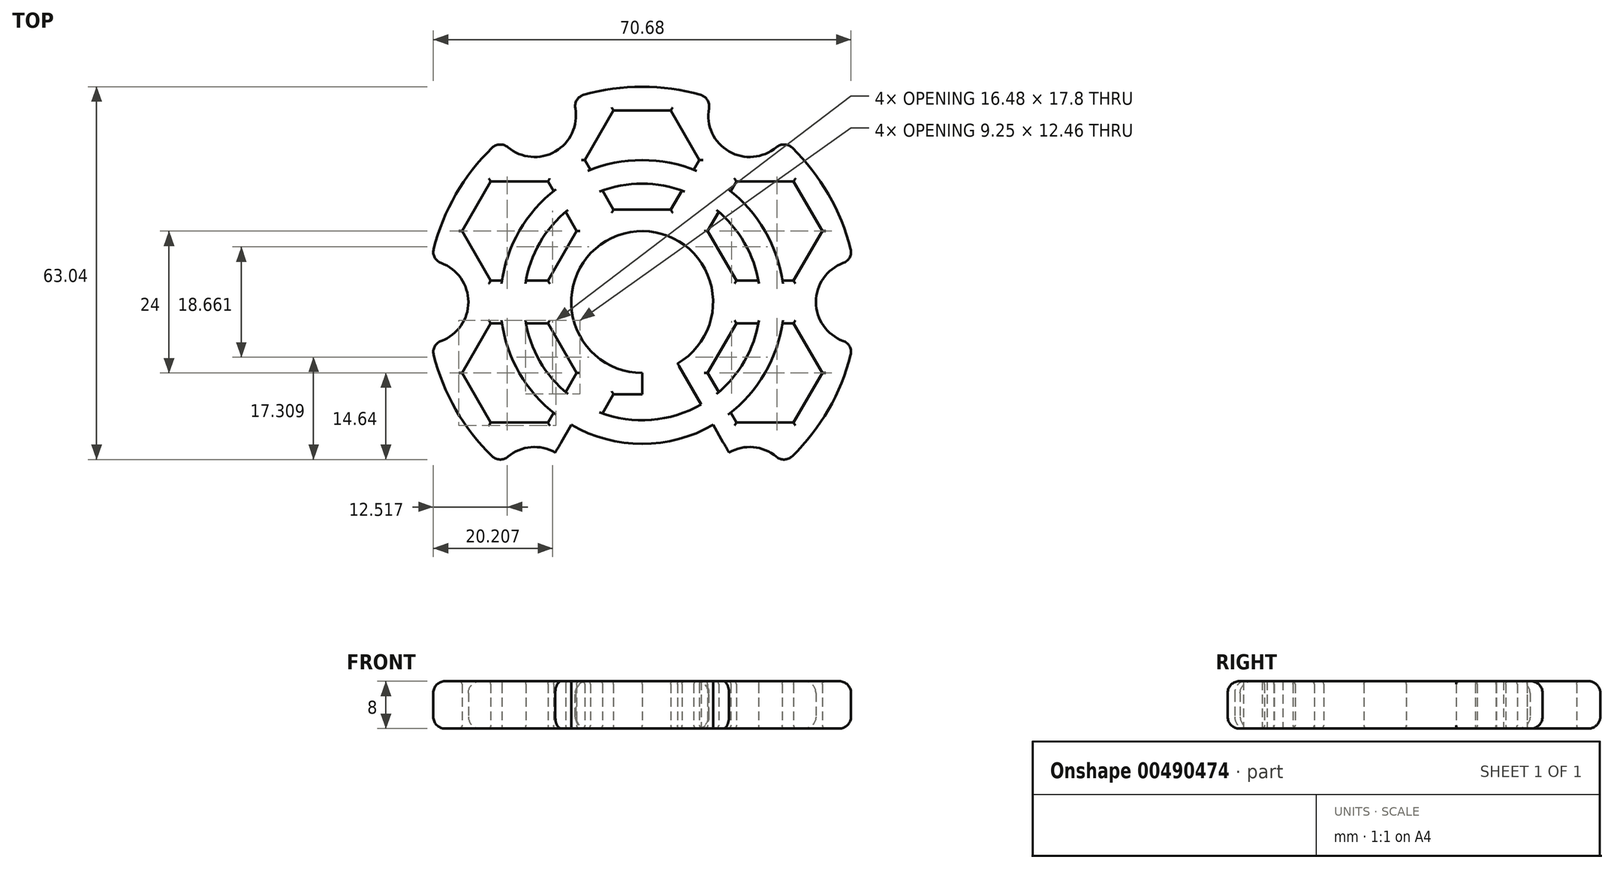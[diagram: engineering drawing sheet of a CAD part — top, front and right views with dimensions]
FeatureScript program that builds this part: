
annotation { "Feature Type Name" : "Feature", "Feature Type Description" : "" }
export const myFeature = defineFeature(function(context is Context, id is Id, definition is map)
    precondition{}
    {
        {
            var Q0;
            Q0=qCreatedBy(makeId("Top.planeOp"),FACE);
            var sketch = newSketch(context, id + "F0", { "sketchPlane" : qUnion([Q0])});
            skCircle(sketch, "E0", {"center": v(0, 0) * mm, "radius": 12 * mm});
            skCircle(sketch, "E1", {"center": v(0, 0) * mm, "radius": 20 * mm});
            skLineSegment(sketch, "E2", {"start": v(0, 0) * mm, "end": v(0, -49.72) * mm});
            skLineSegment(sketch, "E3", {"start": v(0, -49.72) * mm, "end": v(0, 47.4) * mm});
            skLineSegment(sketch, "E4", {"start": v(0, 0) * mm, "end": v(51.5, 29.74) * mm});
            skLineSegment(sketch, "E5", {"start": v(0, 0) * mm, "end": v(-51.59, -29.79) * mm});
            skLineSegment(sketch, "E6", {"start": v(0, 0) * mm, "end": v(55.92, -32.29) * mm});
            skLineSegment(sketch, "E7", {"start": v(0, 0) * mm, "end": v(-48.7, 28.11) * mm});
            skCircle(sketch, "E8", {"center": v(0, 0) * mm, "radius": 24 * mm});
            skCircle(sketch, "E9", {"center": v(0, 0) * mm, "radius": 36.4 * mm});
            skLineSegment(sketch, "E10", {"start": v(0, 0) * mm, "end": v(24.72, 42.82) * mm});
            skLineSegment(sketch, "E11", {"start": v(0, 0) * mm, "end": v(-26.3, -45.55) * mm});
            skLineSegment(sketch, "E12", {"start": v(0, 0) * mm, "end": v(-50.78, 0) * mm});
            skLineSegment(sketch, "E13", {"start": v(0, 0) * mm, "end": v(-24.9, 43.14) * mm});
            skLineSegment(sketch, "E14", {"start": v(0, 0) * mm, "end": v(57.78, 0) * mm});
            skLineSegment(sketch, "E15", {"start": v(0, 0) * mm, "end": v(28.24, -48.92) * mm});
            skCircle(sketch, "E16", {"center": v(18.2, 31.52) * mm, "radius": 7 * mm});
            skCircle(sketch, "E17", {"center": v(36.4, 0) * mm, "radius": 7 * mm});
            skCircle(sketch, "E18", {"center": v(18.2, -31.52) * mm, "radius": 7 * mm});
            skCircle(sketch, "E19", {"center": v(-18.2, -31.52) * mm, "radius": 7 * mm});
            skCircle(sketch, "E20", {"center": v(-36.4, 0) * mm, "radius": 7 * mm});
            skCircle(sketch, "E21", {"center": v(-18.2, 31.52) * mm, "radius": 7 * mm});
            skCircle(sketch, "E22.cCircle", {"center": v(0, -24) * mm, "radius": 8.4 * mm, "construction": true});
            skLineSegment(sketch, "E22.0", {"start": v(-4.85, -15.6) * mm, "end": v(4.85, -15.6) * mm});
            skLineSegment(sketch, "E22.1", {"start": v(4.85, -15.6) * mm, "end": v(9.7, -24) * mm});
            skLineSegment(sketch, "E22.2", {"start": v(9.7, -24) * mm, "end": v(4.85, -32.4) * mm});
            skLineSegment(sketch, "E22.3", {"start": v(4.85, -32.4) * mm, "end": v(-4.85, -32.4) * mm});
            skLineSegment(sketch, "E22.4", {"start": v(-4.85, -32.4) * mm, "end": v(-9.7, -24) * mm});
            skLineSegment(sketch, "E22.5", {"start": v(-9.7, -24) * mm, "end": v(-4.85, -15.6) * mm});
            skPoint(sketch, "E22.0.midPoint", {"position": v(0, -15.6) * mm});
            skCircle(sketch, "E23.cCircle", {"center": v(-20.78, -12) * mm, "radius": 8.4 * mm, "construction": true});
            skLineSegment(sketch, "E23.0", {"start": v(-15.93, -3.6) * mm, "end": v(-11.09, -12) * mm});
            skLineSegment(sketch, "E23.1", {"start": v(-11.09, -12) * mm, "end": v(-15.93, -20.4) * mm});
            skLineSegment(sketch, "E23.2", {"start": v(-15.93, -20.4) * mm, "end": v(-25.63, -20.4) * mm});
            skLineSegment(sketch, "E23.3", {"start": v(-25.63, -20.4) * mm, "end": v(-30.48, -12) * mm});
            skLineSegment(sketch, "E23.4", {"start": v(-30.48, -12) * mm, "end": v(-25.63, -3.6) * mm});
            skLineSegment(sketch, "E23.5", {"start": v(-25.63, -3.6) * mm, "end": v(-15.93, -3.6) * mm});
            skPoint(sketch, "E23.0.midPoint", {"position": v(-13.5, -7.8) * mm});
            skCircle(sketch, "E24.cCircle", {"center": v(-20.78, 12) * mm, "radius": 8.4 * mm, "construction": true});
            skLineSegment(sketch, "E24.0", {"start": v(-11.09, 12) * mm, "end": v(-15.93, 3.6) * mm});
            skLineSegment(sketch, "E24.1", {"start": v(-15.93, 3.6) * mm, "end": v(-25.63, 3.6) * mm});
            skLineSegment(sketch, "E24.2", {"start": v(-25.63, 3.6) * mm, "end": v(-30.48, 12) * mm});
            skLineSegment(sketch, "E24.3", {"start": v(-30.48, 12) * mm, "end": v(-25.63, 20.4) * mm});
            skLineSegment(sketch, "E24.4", {"start": v(-25.63, 20.4) * mm, "end": v(-15.93, 20.4) * mm});
            skLineSegment(sketch, "E24.5", {"start": v(-15.93, 20.4) * mm, "end": v(-11.09, 12) * mm});
            skPoint(sketch, "E24.0.midPoint", {"position": v(-13.5, 7.8) * mm});
            skCircle(sketch, "E25.cCircle", {"center": v(0, 24) * mm, "radius": 8.4 * mm, "construction": true});
            skLineSegment(sketch, "E25.0", {"start": v(4.85, 15.6) * mm, "end": v(-4.85, 15.6) * mm});
            skLineSegment(sketch, "E25.1", {"start": v(-4.85, 15.6) * mm, "end": v(-9.7, 24) * mm});
            skLineSegment(sketch, "E25.2", {"start": v(-9.7, 24) * mm, "end": v(-4.85, 32.4) * mm});
            skLineSegment(sketch, "E25.3", {"start": v(-4.85, 32.4) * mm, "end": v(4.85, 32.4) * mm});
            skLineSegment(sketch, "E25.4", {"start": v(4.85, 32.4) * mm, "end": v(9.7, 24) * mm});
            skLineSegment(sketch, "E25.5", {"start": v(9.7, 24) * mm, "end": v(4.85, 15.6) * mm});
            skPoint(sketch, "E25.0.midPoint", {"position": v(0, 15.6) * mm});
            skCircle(sketch, "E26.cCircle", {"center": v(20.78, 12) * mm, "radius": 8.4 * mm, "construction": true});
            skLineSegment(sketch, "E26.0", {"start": v(15.93, 3.6) * mm, "end": v(11.09, 12) * mm});
            skLineSegment(sketch, "E26.1", {"start": v(11.09, 12) * mm, "end": v(15.93, 20.4) * mm});
            skLineSegment(sketch, "E26.2", {"start": v(15.93, 20.4) * mm, "end": v(25.63, 20.4) * mm});
            skLineSegment(sketch, "E26.3", {"start": v(25.63, 20.4) * mm, "end": v(30.48, 12) * mm});
            skLineSegment(sketch, "E26.4", {"start": v(30.48, 12) * mm, "end": v(25.63, 3.6) * mm});
            skLineSegment(sketch, "E26.5", {"start": v(25.63, 3.6) * mm, "end": v(15.93, 3.6) * mm});
            skPoint(sketch, "E26.0.midPoint", {"position": v(13.5, 7.8) * mm});
            skCircle(sketch, "E27.cCircle", {"center": v(20.78, -12) * mm, "radius": 8.4 * mm, "construction": true});
            skLineSegment(sketch, "E27.0", {"start": v(11.09, -12) * mm, "end": v(15.93, -3.6) * mm});
            skLineSegment(sketch, "E27.1", {"start": v(15.93, -3.6) * mm, "end": v(25.63, -3.6) * mm});
            skLineSegment(sketch, "E27.2", {"start": v(25.63, -3.6) * mm, "end": v(30.48, -12) * mm});
            skLineSegment(sketch, "E27.3", {"start": v(30.48, -12) * mm, "end": v(25.63, -20.4) * mm});
            skLineSegment(sketch, "E27.4", {"start": v(25.63, -20.4) * mm, "end": v(15.93, -20.4) * mm});
            skLineSegment(sketch, "E27.5", {"start": v(15.93, -20.4) * mm, "end": v(11.09, -12) * mm});
            skPoint(sketch, "E27.0.midPoint", {"position": v(13.5, -7.8) * mm});
            skSolve(sketch);
        }
        {
            var Q0;
            {var subQ0=sQuery(id+"F0.wireOp",EDGE,"E9");var subQ1=sQuery(id+"F0.wireOp",EDGE,"E7");var subQ2=makeQuery(id+"F0.imprint","INTERSECT",VERTEX,{"derivedFrom":[subQ1,subQ0]});Q0=makeQuery(id+"F0.imprint","IMPRINT",FACE,{"disambiguationData":[TD([[makeQuery(id+"F0.imprint","IMPRINT",EDGE,{"disambiguationData":[TD([[subQ2,1.0]])],"derivedFrom":subQ1}),1.0]])]});}
            var Q1;
            {var subQ0=sQuery(id+"F0.wireOp",EDGE,"E9");var subQ1=sQuery(id+"F0.wireOp",EDGE,"E7");var subQ2=makeQuery(id+"F0.imprint","INTERSECT",VERTEX,{"derivedFrom":[subQ1,subQ0]});Q1=makeQuery(id+"F0.imprint","IMPRINT",FACE,{"disambiguationData":[TD([[makeQuery(id+"F0.imprint","IMPRINT",EDGE,{"disambiguationData":[TD([[subQ2,1.0]])],"derivedFrom":subQ1}),-1.0]])]});}
            var Q2;
            {var subQ1=sQuery(id+"F0.wireOp",EDGE,"E3");var subQ7=sQuery(id+"F0.wireOp",EDGE,"E9");var subQ8=makeQuery(id+"F0.imprint","INTERSECT",VERTEX,{"disambiguationData":[OD(1.0)],"derivedFrom":[subQ1,subQ7]});Q2=makeQuery(id+"F0.imprint","IMPRINT",FACE,{"disambiguationData":[TD([[makeQuery(id+"F0.imprint","IMPRINT",EDGE,{"disambiguationData":[TD([[subQ8,1.0]])],"derivedFrom":subQ1}),1.0]])]});}
            var Q3;
            {var subQ0=sQuery(id+"F0.wireOp",EDGE,"E9");var subQ1=sQuery(id+"F0.wireOp",EDGE,"E3");var subQ2=makeQuery(id+"F0.imprint","INTERSECT",VERTEX,{"disambiguationData":[OD(1.0)],"derivedFrom":[subQ1,subQ0]});Q3=makeQuery(id+"F0.imprint","IMPRINT",FACE,{"disambiguationData":[TD([[makeQuery(id+"F0.imprint","IMPRINT",EDGE,{"disambiguationData":[TD([[subQ2,1.0]])],"derivedFrom":subQ1}),-1.0]])]});}
            var Q4;
            {var subQ0=sQuery(id+"F0.wireOp",EDGE,"E9");var subQ1=sQuery(id+"F0.wireOp",EDGE,"E4");var subQ2=makeQuery(id+"F0.imprint","INTERSECT",VERTEX,{"derivedFrom":[subQ1,subQ0]});Q4=makeQuery(id+"F0.imprint","IMPRINT",FACE,{"disambiguationData":[TD([[makeQuery(id+"F0.imprint","IMPRINT",EDGE,{"disambiguationData":[TD([[subQ2,1.0]])],"derivedFrom":subQ1}),1.0]])]});}
            var Q5;
            {var subQ1=sQuery(id+"F0.wireOp",EDGE,"E4");var subQ9=sQuery(id+"F0.wireOp",EDGE,"E9");var subQ10=makeQuery(id+"F0.imprint","INTERSECT",VERTEX,{"derivedFrom":[subQ1,subQ9]});Q5=makeQuery(id+"F0.imprint","IMPRINT",FACE,{"disambiguationData":[TD([[makeQuery(id+"F0.imprint","IMPRINT",EDGE,{"disambiguationData":[TD([[subQ10,1.0]])],"derivedFrom":subQ1}),-1.0]])]});}
            var Q6;
            {var subQ0=sQuery(id+"F0.wireOp",EDGE,"E9");var subQ1=sQuery(id+"F0.wireOp",EDGE,"E6");var subQ2=makeQuery(id+"F0.imprint","INTERSECT",VERTEX,{"derivedFrom":[subQ1,subQ0]});Q6=makeQuery(id+"F0.imprint","IMPRINT",FACE,{"disambiguationData":[TD([[makeQuery(id+"F0.imprint","IMPRINT",EDGE,{"disambiguationData":[TD([[subQ2,1.0]])],"derivedFrom":subQ1}),1.0]])]});}
            var Q7;
            {var subQ1=sQuery(id+"F0.wireOp",EDGE,"E6");var subQ5=sQuery(id+"F0.wireOp",EDGE,"E9");var subQ6=makeQuery(id+"F0.imprint","INTERSECT",VERTEX,{"derivedFrom":[subQ1,subQ5]});Q7=makeQuery(id+"F0.imprint","IMPRINT",FACE,{"disambiguationData":[TD([[makeQuery(id+"F0.imprint","IMPRINT",EDGE,{"disambiguationData":[TD([[subQ6,1.0]])],"derivedFrom":subQ1}),-1.0]])]});}
            var Q8;
            {var subQ0=sQuery(id+"F0.wireOp",EDGE,"E9");var subQ1=sQuery(id+"F0.wireOp",EDGE,"E3");var subQ2=makeQuery(id+"F0.imprint","INTERSECT",VERTEX,{"disambiguationData":[OD(0.0)],"derivedFrom":[subQ1,subQ0]});Q8=makeQuery(id+"F0.imprint","IMPRINT",FACE,{"disambiguationData":[TD([[makeQuery(id+"F0.imprint","IMPRINT",EDGE,{"disambiguationData":[TD([[subQ2,-1.0]])],"derivedFrom":subQ1}),-1.0]])]});}
            var Q9;
            {var subQ1=sQuery(id+"F0.wireOp",EDGE,"E3");var subQ7=sQuery(id+"F0.wireOp",EDGE,"E9");var subQ8=makeQuery(id+"F0.imprint","INTERSECT",VERTEX,{"disambiguationData":[OD(0.0)],"derivedFrom":[subQ1,subQ7]});Q9=makeQuery(id+"F0.imprint","IMPRINT",FACE,{"disambiguationData":[TD([[makeQuery(id+"F0.imprint","IMPRINT",EDGE,{"disambiguationData":[TD([[subQ8,-1.0]])],"derivedFrom":subQ1}),1.0]])]});}
            var Q10;
            {var subQ0=sQuery(id+"F0.wireOp",EDGE,"E9");var subQ1=sQuery(id+"F0.wireOp",EDGE,"E5");var subQ2=makeQuery(id+"F0.imprint","INTERSECT",VERTEX,{"derivedFrom":[subQ1,subQ0]});Q10=makeQuery(id+"F0.imprint","IMPRINT",FACE,{"disambiguationData":[TD([[makeQuery(id+"F0.imprint","IMPRINT",EDGE,{"disambiguationData":[TD([[subQ2,1.0]])],"derivedFrom":subQ1}),1.0]])]});}
            var Q11;
            {var subQ0=sQuery(id+"F0.wireOp",EDGE,"E9");var subQ1=sQuery(id+"F0.wireOp",EDGE,"E5");var subQ2=makeQuery(id+"F0.imprint","INTERSECT",VERTEX,{"derivedFrom":[subQ1,subQ0]});Q11=makeQuery(id+"F0.imprint","IMPRINT",FACE,{"disambiguationData":[TD([[makeQuery(id+"F0.imprint","IMPRINT",EDGE,{"disambiguationData":[TD([[subQ2,1.0]])],"derivedFrom":subQ1}),-1.0]])]});}
            var Q12;
            {var subQ0=sQuery(id+"F0.wireOp",EDGE,"E12");var subQ5=sQuery(id+"F0.wireOp",EDGE,"E8");var subQ7=makeQuery(id+"F0.imprint","INTERSECT",VERTEX,{"derivedFrom":[subQ5,subQ0]});Q12=makeQuery(id+"F0.imprint","IMPRINT",FACE,{"disambiguationData":[TD([[makeQuery(id+"F0.imprint","IMPRINT",EDGE,{"disambiguationData":[TD([[subQ7,-1.0]])],"derivedFrom":subQ5}),1.0]])]});}
            var Q13;
            {var subQ0=sQuery(id+"F0.wireOp",EDGE,"E12");var subQ1=sQuery(id+"F0.wireOp",EDGE,"E0");var subQ2=makeQuery(id+"F0.imprint","INTERSECT",VERTEX,{"derivedFrom":[subQ1,subQ0]});Q13=makeQuery(id+"F0.imprint","IMPRINT",FACE,{"disambiguationData":[TD([[makeQuery(id+"F0.imprint","IMPRINT",EDGE,{"disambiguationData":[TD([[subQ2,-1.0]])],"derivedFrom":subQ1}),-1.0]])]});}
            var Q14;
            {var subQ0=sQuery(id+"F0.wireOp",EDGE,"E7");var subQ1=sQuery(id+"F0.wireOp",EDGE,"E0");var subQ2=makeQuery(id+"F0.imprint","INTERSECT",VERTEX,{"derivedFrom":[subQ1,subQ0]});Q14=makeQuery(id+"F0.imprint","IMPRINT",FACE,{"disambiguationData":[TD([[makeQuery(id+"F0.imprint","IMPRINT",EDGE,{"disambiguationData":[TD([[subQ2,-1.0]])],"derivedFrom":subQ1}),-1.0]])]});}
            var Q15;
            {var subQ3=sQuery(id+"F0.wireOp",EDGE,"NqLbyCLt-QwBI-9MIB-e1Nx-km0DvbRRgn6a");var subQ5=sQuery(id+"F0.wireOp",EDGE,"E8");var subQ6=makeQuery(id+"F0.imprint","INTERSECT",VERTEX,{"disambiguationData":[OD(1.0)],"derivedFrom":[subQ5,subQ3]});Q15=makeQuery(id+"F0.imprint","IMPRINT",FACE,{"disambiguationData":[TD([[makeQuery(id+"F0.imprint","IMPRINT",EDGE,{"disambiguationData":[TD([[subQ6,-1.0]])],"derivedFrom":subQ5}),1.0]])]});}
            var Q16;
            {var subQ0=sQuery(id+"F0.wireOp",EDGE,"E13");var subQ5=sQuery(id+"F0.wireOp",EDGE,"E8");var subQ7=makeQuery(id+"F0.imprint","INTERSECT",VERTEX,{"derivedFrom":[subQ5,subQ0]});Q16=makeQuery(id+"F0.imprint","IMPRINT",FACE,{"disambiguationData":[TD([[makeQuery(id+"F0.imprint","IMPRINT",EDGE,{"disambiguationData":[TD([[subQ7,-1.0]])],"derivedFrom":subQ5}),1.0]])]});}
            var Q17;
            {var subQ0=sQuery(id+"F0.wireOp",EDGE,"E3");var subQ1=sQuery(id+"F0.wireOp",EDGE,"E0");var subQ2=makeQuery(id+"F0.imprint","INTERSECT",VERTEX,{"disambiguationData":[OD(0.0)],"derivedFrom":[subQ1,subQ0]});Q17=makeQuery(id+"F0.imprint","IMPRINT",FACE,{"disambiguationData":[TD([[makeQuery(id+"F0.imprint","IMPRINT",EDGE,{"disambiguationData":[TD([[subQ2,-1.0]])],"derivedFrom":subQ1}),-1.0]])]});}
            var Q18;
            {var subQ0=sQuery(id+"F0.wireOp",EDGE,"E10");var subQ5=sQuery(id+"F0.wireOp",EDGE,"E8");var subQ7=makeQuery(id+"F0.imprint","INTERSECT",VERTEX,{"derivedFrom":[subQ5,subQ0]});Q18=makeQuery(id+"F0.imprint","IMPRINT",FACE,{"disambiguationData":[TD([[makeQuery(id+"F0.imprint","IMPRINT",EDGE,{"disambiguationData":[TD([[subQ7,-1.0]])],"derivedFrom":subQ5}),1.0]])]});}
            var Q19;
            {var subQ0=sQuery(id+"F0.wireOp",EDGE,"E10");var subQ1=sQuery(id+"F0.wireOp",EDGE,"E0");var subQ2=makeQuery(id+"F0.imprint","INTERSECT",VERTEX,{"derivedFrom":[subQ1,subQ0]});Q19=makeQuery(id+"F0.imprint","IMPRINT",FACE,{"disambiguationData":[TD([[makeQuery(id+"F0.imprint","IMPRINT",EDGE,{"disambiguationData":[TD([[subQ2,-1.0]])],"derivedFrom":subQ1}),-1.0]])]});}
            var Q20;
            {var subQ0=sQuery(id+"F0.wireOp",EDGE,"E4");var subQ1=sQuery(id+"F0.wireOp",EDGE,"E0");var subQ2=makeQuery(id+"F0.imprint","INTERSECT",VERTEX,{"derivedFrom":[subQ1,subQ0]});Q20=makeQuery(id+"F0.imprint","IMPRINT",FACE,{"disambiguationData":[TD([[makeQuery(id+"F0.imprint","IMPRINT",EDGE,{"disambiguationData":[TD([[subQ2,-1.0]])],"derivedFrom":subQ1}),-1.0]])]});}
            var Q21;
            {var subQ3=sQuery(id+"F0.wireOp",EDGE,"33CorVpG-yTT2-nvUV-cjIG-PMlhWEX7tbI9");var subQ5=sQuery(id+"F0.wireOp",EDGE,"E8");var subQ7=makeQuery(id+"F0.imprint","INTERSECT",VERTEX,{"disambiguationData":[OD(1.0)],"derivedFrom":[subQ5,subQ3]});Q21=makeQuery(id+"F0.imprint","IMPRINT",FACE,{"disambiguationData":[TD([[makeQuery(id+"F0.imprint","IMPRINT",EDGE,{"disambiguationData":[TD([[subQ7,-1.0]])],"derivedFrom":subQ5}),1.0]])]});}
            var Q22;
            {var subQ3=sQuery(id+"F0.wireOp",EDGE,"33CorVpG-yTT2-nvUV-cjIG-PMlhWEX7tbI9");var subQ5=sQuery(id+"F0.wireOp",EDGE,"E8");var subQ7=makeQuery(id+"F0.imprint","INTERSECT",VERTEX,{"disambiguationData":[OD(0.0)],"derivedFrom":[subQ5,subQ3]});Q22=makeQuery(id+"F0.imprint","IMPRINT",FACE,{"disambiguationData":[TD([[makeQuery(id+"F0.imprint","IMPRINT",EDGE,{"disambiguationData":[TD([[subQ7,1.0]])],"derivedFrom":subQ5}),1.0]])]});}
            var Q23;
            {var subQ0=sQuery(id+"F0.wireOp",EDGE,"E4");var subQ1=sQuery(id+"F0.wireOp",EDGE,"E0");var subQ2=makeQuery(id+"F0.imprint","INTERSECT",VERTEX,{"derivedFrom":[subQ1,subQ0]});Q23=makeQuery(id+"F0.imprint","IMPRINT",FACE,{"disambiguationData":[TD([[makeQuery(id+"F0.imprint","IMPRINT",EDGE,{"disambiguationData":[TD([[subQ2,1.0]])],"derivedFrom":subQ1}),-1.0]])]});}
            var Q24;
            {var subQ0=sQuery(id+"F0.wireOp",EDGE,"E14");var subQ1=sQuery(id+"F0.wireOp",EDGE,"E0");var subQ2=makeQuery(id+"F0.imprint","INTERSECT",VERTEX,{"derivedFrom":[subQ1,subQ0]});Q24=makeQuery(id+"F0.imprint","IMPRINT",FACE,{"disambiguationData":[TD([[makeQuery(id+"F0.imprint","IMPRINT",EDGE,{"disambiguationData":[TD([[subQ2,1.0]])],"derivedFrom":subQ1}),-1.0]])]});}
            var Q25;
            {var subQ0=sQuery(id+"F0.wireOp",EDGE,"E14");var subQ5=sQuery(id+"F0.wireOp",EDGE,"E8");var subQ6=makeQuery(id+"F0.imprint","INTERSECT",VERTEX,{"derivedFrom":[subQ5,subQ0]});Q25=makeQuery(id+"F0.imprint","IMPRINT",FACE,{"disambiguationData":[TD([[makeQuery(id+"F0.imprint","IMPRINT",EDGE,{"disambiguationData":[TD([[subQ6,1.0]])],"derivedFrom":subQ5}),1.0]])]});}
            var Q26;
            {var subQ0=sQuery(id+"F0.wireOp",EDGE,"E15");var subQ5=sQuery(id+"F0.wireOp",EDGE,"E8");var subQ6=makeQuery(id+"F0.imprint","INTERSECT",VERTEX,{"derivedFrom":[subQ5,subQ0]});Q26=makeQuery(id+"F0.imprint","IMPRINT",FACE,{"disambiguationData":[TD([[makeQuery(id+"F0.imprint","IMPRINT",EDGE,{"disambiguationData":[TD([[subQ6,-1.0]])],"derivedFrom":subQ5}),1.0]])]});}
            var Q27;
            {var subQ0=sQuery(id+"F0.wireOp",EDGE,"E15");var subQ1=sQuery(id+"F0.wireOp",EDGE,"E0");var subQ2=makeQuery(id+"F0.imprint","INTERSECT",VERTEX,{"derivedFrom":[subQ1,subQ0]});Q27=makeQuery(id+"F0.imprint","IMPRINT",FACE,{"disambiguationData":[TD([[makeQuery(id+"F0.imprint","IMPRINT",EDGE,{"disambiguationData":[TD([[subQ2,-1.0]])],"derivedFrom":subQ1}),-1.0]])]});}
            var Q28;
            {var subQ3=sQuery(id+"F0.wireOp",EDGE,"Z31AIPb3-Qnal-9L9K-KWPF-0pA5MV0Y2tzz");var subQ5=sQuery(id+"F0.wireOp",EDGE,"E8");var subQ6=makeQuery(id+"F0.imprint","INTERSECT",VERTEX,{"disambiguationData":[OD(1.0)],"derivedFrom":[subQ5,subQ3]});Q28=makeQuery(id+"F0.imprint","IMPRINT",FACE,{"disambiguationData":[TD([[makeQuery(id+"F0.imprint","IMPRINT",EDGE,{"disambiguationData":[TD([[subQ6,-1.0]])],"derivedFrom":subQ5}),1.0]])]});}
            var Q29;
            {var subQ0=sQuery(id+"F0.wireOp",EDGE,"E3");var subQ1=sQuery(id+"F0.wireOp",EDGE,"E0");var subQ2=makeQuery(id+"F0.imprint","INTERSECT",VERTEX,{"disambiguationData":[OD(1.0)],"derivedFrom":[subQ1,subQ0]});Q29=makeQuery(id+"F0.imprint","IMPRINT",FACE,{"disambiguationData":[TD([[makeQuery(id+"F0.imprint","IMPRINT",EDGE,{"disambiguationData":[TD([[subQ2,-1.0]])],"derivedFrom":subQ1}),-1.0]])]});}
            var Q30;
            {var subQ0=sQuery(id+"F0.wireOp",EDGE,"E11");var subQ5=sQuery(id+"F0.wireOp",EDGE,"E8");var subQ6=makeQuery(id+"F0.imprint","INTERSECT",VERTEX,{"derivedFrom":[subQ5,subQ0]});Q30=makeQuery(id+"F0.imprint","IMPRINT",FACE,{"disambiguationData":[TD([[makeQuery(id+"F0.imprint","IMPRINT",EDGE,{"disambiguationData":[TD([[subQ6,-1.0]])],"derivedFrom":subQ5}),1.0]])]});}
            var Q31;
            {var subQ0=sQuery(id+"F0.wireOp",EDGE,"E11");var subQ1=sQuery(id+"F0.wireOp",EDGE,"E0");var subQ2=makeQuery(id+"F0.imprint","INTERSECT",VERTEX,{"derivedFrom":[subQ1,subQ0]});Q31=makeQuery(id+"F0.imprint","IMPRINT",FACE,{"disambiguationData":[TD([[makeQuery(id+"F0.imprint","IMPRINT",EDGE,{"disambiguationData":[TD([[subQ2,-1.0]])],"derivedFrom":subQ1}),-1.0]])]});}
            var Q32;
            {var subQ0=sQuery(id+"F0.wireOp",EDGE,"E5");var subQ1=sQuery(id+"F0.wireOp",EDGE,"E0");var subQ2=makeQuery(id+"F0.imprint","INTERSECT",VERTEX,{"derivedFrom":[subQ1,subQ0]});Q32=makeQuery(id+"F0.imprint","IMPRINT",FACE,{"disambiguationData":[TD([[makeQuery(id+"F0.imprint","IMPRINT",EDGE,{"disambiguationData":[TD([[subQ2,-1.0]])],"derivedFrom":subQ1}),-1.0]])]});}
            var Q33;
            {var subQ0=sQuery(id+"F0.wireOp",EDGE,"E13");var subQ1=sQuery(id+"F0.wireOp",EDGE,"E0");var subQ2=makeQuery(id+"F0.imprint","INTERSECT",VERTEX,{"derivedFrom":[subQ1,subQ0]});Q33=makeQuery(id+"F0.imprint","IMPRINT",FACE,{"disambiguationData":[TD([[makeQuery(id+"F0.imprint","IMPRINT",EDGE,{"disambiguationData":[TD([[subQ2,-1.0]])],"derivedFrom":subQ1}),-1.0]])]});}
            var Q34;
            {var subQ3=sQuery(id+"F0.wireOp",EDGE,"FrVRpejz-aWTZ-dKt5-0AgZ-ki6dz13qyr7O");var subQ5=sQuery(id+"F0.wireOp",EDGE,"E8");var subQ6=makeQuery(id+"F0.imprint","INTERSECT",VERTEX,{"disambiguationData":[OD(1.0)],"derivedFrom":[subQ5,subQ3]});Q34=makeQuery(id+"F0.imprint","IMPRINT",FACE,{"disambiguationData":[TD([[makeQuery(id+"F0.imprint","IMPRINT",EDGE,{"disambiguationData":[TD([[subQ6,-1.0]])],"derivedFrom":subQ5}),1.0]])]});}
            var Q35;
            {var subQ3=sQuery(id+"F0.wireOp",EDGE,"PnXZhhwe-JsCa-7CxD-iQOa-k5J0qBTIRsT0");var subQ5=sQuery(id+"F0.wireOp",EDGE,"E8");var subQ6=makeQuery(id+"F0.imprint","INTERSECT",VERTEX,{"disambiguationData":[OD(1.0)],"derivedFrom":[subQ5,subQ3]});Q35=makeQuery(id+"F0.imprint","IMPRINT",FACE,{"disambiguationData":[TD([[makeQuery(id+"F0.imprint","IMPRINT",EDGE,{"disambiguationData":[TD([[subQ6,-1.0]])],"derivedFrom":subQ5}),1.0]])]});}
            var Q36;
            {var subQ0=sQuery(id+"F0.wireOp",EDGE,"E26.5");var subQ1=sQuery(id+"F0.wireOp",EDGE,"E1");var subQ2=makeQuery(id+"F0.imprint","INTERSECT",VERTEX,{"derivedFrom":[subQ1,subQ0]});Q36=makeQuery(id+"F0.imprint","IMPRINT",FACE,{"disambiguationData":[TD([[makeQuery(id+"F0.imprint","IMPRINT",EDGE,{"disambiguationData":[TD([[subQ2,1.0]])],"derivedFrom":subQ1}),-1.0]])]});}
            var Q37;
            {var subQ0=sQuery(id+"F0.wireOp",EDGE,"E22.1");var subQ1=sQuery(id+"F0.wireOp",EDGE,"E1");var subQ2=makeQuery(id+"F0.imprint","INTERSECT",VERTEX,{"derivedFrom":[subQ1,subQ0]});Q37=makeQuery(id+"F0.imprint","IMPRINT",FACE,{"disambiguationData":[TD([[makeQuery(id+"F0.imprint","IMPRINT",EDGE,{"disambiguationData":[TD([[subQ2,-1.0]])],"derivedFrom":subQ1}),-1.0]])]});}
            var Q38;
            {var subQ0=sQuery(id+"F0.wireOp",EDGE,"E24.1");var subQ1=sQuery(id+"F0.wireOp",EDGE,"E1");var subQ2=makeQuery(id+"F0.imprint","INTERSECT",VERTEX,{"derivedFrom":[subQ1,subQ0]});Q38=makeQuery(id+"F0.imprint","IMPRINT",FACE,{"disambiguationData":[TD([[makeQuery(id+"F0.imprint","IMPRINT",EDGE,{"disambiguationData":[TD([[subQ2,-1.0]])],"derivedFrom":subQ1}),-1.0]])]});}
            var Q39;
            {var subQ0=sQuery(id+"F0.wireOp",EDGE,"E23.1");var subQ1=sQuery(id+"F0.wireOp",EDGE,"E1");var subQ2=makeQuery(id+"F0.imprint","INTERSECT",VERTEX,{"derivedFrom":[subQ1,subQ0]});Q39=makeQuery(id+"F0.imprint","IMPRINT",FACE,{"disambiguationData":[TD([[makeQuery(id+"F0.imprint","IMPRINT",EDGE,{"disambiguationData":[TD([[subQ2,-1.0]])],"derivedFrom":subQ1}),-1.0]])]});}
            var Q40;
            {var subQ0=sQuery(id+"F0.wireOp",EDGE,"E25.1");var subQ1=sQuery(id+"F0.wireOp",EDGE,"E1");var subQ2=makeQuery(id+"F0.imprint","INTERSECT",VERTEX,{"derivedFrom":[subQ1,subQ0]});Q40=makeQuery(id+"F0.imprint","IMPRINT",FACE,{"disambiguationData":[TD([[makeQuery(id+"F0.imprint","IMPRINT",EDGE,{"disambiguationData":[TD([[subQ2,-1.0]])],"derivedFrom":subQ1}),-1.0]])]});}
            var Q41;
            {var subQ0=sQuery(id+"F0.wireOp",EDGE,"E26.1");var subQ1=sQuery(id+"F0.wireOp",EDGE,"E1");var subQ2=makeQuery(id+"F0.imprint","INTERSECT",VERTEX,{"derivedFrom":[subQ1,subQ0]});Q41=makeQuery(id+"F0.imprint","IMPRINT",FACE,{"disambiguationData":[TD([[makeQuery(id+"F0.imprint","IMPRINT",EDGE,{"disambiguationData":[TD([[subQ2,-1.0]])],"derivedFrom":subQ1}),-1.0]])]});}
            extrude(context, id + "F1", {"entities" : qUnion([Q0, Q1, Q2, Q3, Q4, Q5, Q6, Q7, Q8, Q9, Q10, Q11, Q12, Q13, Q14, Q15, Q16, Q17, Q18, Q19, Q20, Q21, Q22, Q23, Q24, Q25, Q26, Q27, Q28, Q29, Q30, Q31, Q32, Q33, Q34, Q35, Q36, Q37, Q38, Q39, Q40, Q41]), "depth" : 8 * mm});
        }
        {
            var Q0;
            Q0=makeQuery(id+"F1.opExtrude","CAP_EDGE",EDGE,{"disambiguationData":[OSD([sQuery(id+"F0.wireOp",EDGE,"NqLbyCLt-QwBI-9MIB-e1Nx-km0DvbRRgn6a")])],"isStart":false});
            var Q1;
            Q1=makeQuery(id+"F1.opExtrude","CAP_EDGE",EDGE,{"disambiguationData":[OSD([sQuery(id+"F0.wireOp",EDGE,"FrVRpejz-aWTZ-dKt5-0AgZ-ki6dz13qyr7O")])],"isStart":false});
            var Q2;
            Q2=makeQuery(id+"F1.opExtrude","CAP_EDGE",EDGE,{"disambiguationData":[OSD([sQuery(id+"F0.wireOp",EDGE,"33CorVpG-yTT2-nvUV-cjIG-PMlhWEX7tbI9")])],"isStart":false});
            var Q3;
            Q3=makeQuery(id+"F1.opExtrude","CAP_EDGE",EDGE,{"disambiguationData":[OSD([sQuery(id+"F0.wireOp",EDGE,"ybPrvi5P-VunJ-4jWC-Pnkx-XrBZV12RTwSU")])],"isStart":false});
            var Q4;
            Q4=makeQuery(id+"F1.opExtrude","CAP_EDGE",EDGE,{"disambiguationData":[OSD([sQuery(id+"F0.wireOp",EDGE,"Z31AIPb3-Qnal-9L9K-KWPF-0pA5MV0Y2tzz")])],"isStart":false});
            var Q5;
            Q5=makeQuery(id+"F1.opExtrude","CAP_EDGE",EDGE,{"disambiguationData":[OSD([sQuery(id+"F0.wireOp",EDGE,"PnXZhhwe-JsCa-7CxD-iQOa-k5J0qBTIRsT0")])],"isStart":false});
            var Q6;
            Q6=makeQuery(id+"F1.opExtrude","CAP_EDGE",EDGE,{"disambiguationData":[OSD([sQuery(id+"F0.wireOp",EDGE,"E20")])],"isStart":false});
            var Q7;
            Q7=makeQuery(id+"F1.opExtrude","CAP_EDGE",EDGE,{"disambiguationData":[OSD([sQuery(id+"F0.wireOp",EDGE,"E21")])],"isStart":false});
            var Q8;
            Q8=makeQuery(id+"F1.opExtrude","CAP_EDGE",EDGE,{"disambiguationData":[OSD([sQuery(id+"F0.wireOp",EDGE,"E16")])],"isStart":false});
            var Q9;
            Q9=makeQuery(id+"F1.opExtrude","CAP_EDGE",EDGE,{"disambiguationData":[OSD([sQuery(id+"F0.wireOp",EDGE,"E17")])],"isStart":false});
            var Q10;
            Q10=makeQuery(id+"F1.opExtrude","CAP_EDGE",EDGE,{"disambiguationData":[OSD([sQuery(id+"F0.wireOp",EDGE,"E18")])],"isStart":false});
            var Q11;
            Q11=makeQuery(id+"F1.opExtrude","CAP_EDGE",EDGE,{"disambiguationData":[OSD([sQuery(id+"F0.wireOp",EDGE,"E19")])],"isStart":false});
            var Q12;
            {var subQ0=sQuery(id+"F0.wireOp",EDGE,"E9");var subQ1=makeQuery(id+"F0.imprint","INTERSECT",VERTEX,{"derivedFrom":[sQuery(id+"F0.wireOp",EDGE,"E7"),subQ0]});Q12=makeQuery(id+"F1.opExtrude","CAP_EDGE",EDGE,{"disambiguationData":[OSD([subQ0]),TDD([makeQuery(id+"F0.imprint","IMPRINT",EDGE,{"disambiguationData":[TD([[subQ1,1.0]])],"derivedFrom":subQ0}),makeQuery(id+"F0.imprint","IMPRINT",EDGE,{"disambiguationData":[TD([[subQ1,-1.0]])],"derivedFrom":subQ0})])],"isStart":false});}
            var Q13;
            {var subQ0=sQuery(id+"F0.wireOp",EDGE,"E9");var subQ1=makeQuery(id+"F0.imprint","INTERSECT",VERTEX,{"disambiguationData":[OD(1.0)],"derivedFrom":[sQuery(id+"F0.wireOp",EDGE,"E3"),subQ0]});Q13=makeQuery(id+"F1.opExtrude","CAP_EDGE",EDGE,{"disambiguationData":[OSD([subQ0]),TDD([makeQuery(id+"F0.imprint","IMPRINT",EDGE,{"disambiguationData":[TD([[subQ1,1.0]])],"derivedFrom":subQ0}),makeQuery(id+"F0.imprint","IMPRINT",EDGE,{"disambiguationData":[TD([[subQ1,-1.0]])],"derivedFrom":subQ0})])],"isStart":false});}
            var Q14;
            {var subQ0=sQuery(id+"F0.wireOp",EDGE,"E9");var subQ1=makeQuery(id+"F0.imprint","INTERSECT",VERTEX,{"derivedFrom":[sQuery(id+"F0.wireOp",EDGE,"E4"),subQ0]});Q14=makeQuery(id+"F1.opExtrude","CAP_EDGE",EDGE,{"disambiguationData":[OSD([subQ0]),TDD([makeQuery(id+"F0.imprint","IMPRINT",EDGE,{"disambiguationData":[TD([[subQ1,1.0]])],"derivedFrom":subQ0}),makeQuery(id+"F0.imprint","IMPRINT",EDGE,{"disambiguationData":[TD([[subQ1,-1.0]])],"derivedFrom":subQ0})])],"isStart":false});}
            var Q15;
            {var subQ0=sQuery(id+"F0.wireOp",EDGE,"E9");var subQ1=makeQuery(id+"F0.imprint","INTERSECT",VERTEX,{"derivedFrom":[sQuery(id+"F0.wireOp",EDGE,"E6"),subQ0]});Q15=makeQuery(id+"F1.opExtrude","CAP_EDGE",EDGE,{"disambiguationData":[OSD([subQ0]),TDD([makeQuery(id+"F0.imprint","IMPRINT",EDGE,{"disambiguationData":[TD([[subQ1,1.0]])],"derivedFrom":subQ0}),makeQuery(id+"F0.imprint","IMPRINT",EDGE,{"disambiguationData":[TD([[subQ1,-1.0]])],"derivedFrom":subQ0})])],"isStart":false});}
            var Q16;
            {var subQ0=sQuery(id+"F0.wireOp",EDGE,"E9");var subQ1=makeQuery(id+"F0.imprint","INTERSECT",VERTEX,{"disambiguationData":[OD(0.0)],"derivedFrom":[sQuery(id+"F0.wireOp",EDGE,"E3"),subQ0]});Q16=makeQuery(id+"F1.opExtrude","CAP_EDGE",EDGE,{"disambiguationData":[OSD([subQ0]),TDD([makeQuery(id+"F0.imprint","IMPRINT",EDGE,{"disambiguationData":[TD([[subQ1,1.0]])],"derivedFrom":subQ0}),makeQuery(id+"F0.imprint","IMPRINT",EDGE,{"disambiguationData":[TD([[subQ1,-1.0]])],"derivedFrom":subQ0})])],"isStart":false});}
            var Q17;
            {var subQ0=sQuery(id+"F0.wireOp",EDGE,"E9");var subQ1=makeQuery(id+"F0.imprint","INTERSECT",VERTEX,{"derivedFrom":[sQuery(id+"F0.wireOp",EDGE,"E5"),subQ0]});Q17=makeQuery(id+"F1.opExtrude","CAP_EDGE",EDGE,{"disambiguationData":[OSD([subQ0]),TDD([makeQuery(id+"F0.imprint","IMPRINT",EDGE,{"disambiguationData":[TD([[subQ1,1.0]])],"derivedFrom":subQ0}),makeQuery(id+"F0.imprint","IMPRINT",EDGE,{"disambiguationData":[TD([[subQ1,-1.0]])],"derivedFrom":subQ0})])],"isStart":false});}
            fillet(context, id + "F2", {"entities" : qUnion([Q0, Q1, Q2, Q3, Q4, Q5, Q6, Q7, Q8, Q9, Q10, Q11, Q12, Q13, Q14, Q15, Q16, Q17]), "radius" : 2 * mm, "tangentPropagation" : true, "allowEdgeOverflow" : false});
        }
        {
            var Q0;
            {var subQ0=sQuery(id+"F0.wireOp",EDGE,"E21");var subQ1=sQuery(id+"F0.wireOp",EDGE,"E9");Q0=makeQuery(id+"F1.opExtrude","SWEPT_EDGE",EDGE,{"disambiguationData":[OSD([subQ1,subQ0]),TDD([makeQuery(id+"F0.imprint","INTERSECT",VERTEX,{"disambiguationData":[OD(0.0)],"derivedFrom":[subQ1,subQ0]})])]});}
            var Q1;
            {var subQ0=sQuery(id+"F0.wireOp",EDGE,"E21");var subQ1=sQuery(id+"F0.wireOp",EDGE,"E9");Q1=makeQuery(id+"F1.opExtrude","SWEPT_EDGE",EDGE,{"disambiguationData":[OSD([subQ1,subQ0]),TDD([makeQuery(id+"F0.imprint","INTERSECT",VERTEX,{"disambiguationData":[OD(1.0)],"derivedFrom":[subQ1,subQ0]})])]});}
            var Q2;
            {var subQ0=sQuery(id+"F0.wireOp",EDGE,"E16");var subQ1=sQuery(id+"F0.wireOp",EDGE,"E9");Q2=makeQuery(id+"F1.opExtrude","SWEPT_EDGE",EDGE,{"disambiguationData":[OSD([subQ1,subQ0]),TDD([makeQuery(id+"F0.imprint","INTERSECT",VERTEX,{"disambiguationData":[OD(0.0)],"derivedFrom":[subQ1,subQ0]})])]});}
            var Q3;
            {var subQ0=sQuery(id+"F0.wireOp",EDGE,"E16");var subQ1=sQuery(id+"F0.wireOp",EDGE,"E9");Q3=makeQuery(id+"F1.opExtrude","SWEPT_EDGE",EDGE,{"disambiguationData":[OSD([subQ1,subQ0]),TDD([makeQuery(id+"F0.imprint","INTERSECT",VERTEX,{"disambiguationData":[OD(1.0)],"derivedFrom":[subQ1,subQ0]})])]});}
            var Q4;
            {var subQ0=sQuery(id+"F0.wireOp",EDGE,"E17");var subQ1=sQuery(id+"F0.wireOp",EDGE,"E9");Q4=makeQuery(id+"F1.opExtrude","SWEPT_EDGE",EDGE,{"disambiguationData":[OSD([subQ1,subQ0]),TDD([makeQuery(id+"F0.imprint","INTERSECT",VERTEX,{"disambiguationData":[OD(0.0)],"derivedFrom":[subQ1,subQ0]})])]});}
            var Q5;
            {var subQ0=sQuery(id+"F0.wireOp",EDGE,"E17");var subQ1=sQuery(id+"F0.wireOp",EDGE,"E9");Q5=makeQuery(id+"F1.opExtrude","SWEPT_EDGE",EDGE,{"disambiguationData":[OSD([subQ1,subQ0]),TDD([makeQuery(id+"F0.imprint","INTERSECT",VERTEX,{"disambiguationData":[OD(1.0)],"derivedFrom":[subQ1,subQ0]})])]});}
            var Q6;
            {var subQ0=sQuery(id+"F0.wireOp",EDGE,"E18");var subQ1=sQuery(id+"F0.wireOp",EDGE,"E9");Q6=makeQuery(id+"F1.opExtrude","SWEPT_EDGE",EDGE,{"disambiguationData":[OSD([subQ1,subQ0]),TDD([makeQuery(id+"F0.imprint","INTERSECT",VERTEX,{"disambiguationData":[OD(1.0)],"derivedFrom":[subQ1,subQ0]})])]});}
            var Q7;
            {var subQ0=sQuery(id+"F0.wireOp",EDGE,"E18");var subQ1=sQuery(id+"F0.wireOp",EDGE,"E9");Q7=makeQuery(id+"F1.opExtrude","SWEPT_EDGE",EDGE,{"disambiguationData":[OSD([subQ1,subQ0]),TDD([makeQuery(id+"F0.imprint","INTERSECT",VERTEX,{"disambiguationData":[OD(0.0)],"derivedFrom":[subQ1,subQ0]})])]});}
            var Q8;
            {var subQ0=sQuery(id+"F0.wireOp",EDGE,"E19");var subQ1=sQuery(id+"F0.wireOp",EDGE,"E9");Q8=makeQuery(id+"F1.opExtrude","SWEPT_EDGE",EDGE,{"disambiguationData":[OSD([subQ1,subQ0]),TDD([makeQuery(id+"F0.imprint","INTERSECT",VERTEX,{"disambiguationData":[OD(1.0)],"derivedFrom":[subQ1,subQ0]})])]});}
            var Q9;
            {var subQ0=sQuery(id+"F0.wireOp",EDGE,"E19");var subQ1=sQuery(id+"F0.wireOp",EDGE,"E9");Q9=makeQuery(id+"F1.opExtrude","SWEPT_EDGE",EDGE,{"disambiguationData":[OSD([subQ1,subQ0]),TDD([makeQuery(id+"F0.imprint","INTERSECT",VERTEX,{"disambiguationData":[OD(0.0)],"derivedFrom":[subQ1,subQ0]})])]});}
            var Q10;
            {var subQ0=sQuery(id+"F0.wireOp",EDGE,"E20");var subQ1=sQuery(id+"F0.wireOp",EDGE,"E9");Q10=makeQuery(id+"F1.opExtrude","SWEPT_EDGE",EDGE,{"disambiguationData":[OSD([subQ1,subQ0]),TDD([makeQuery(id+"F0.imprint","INTERSECT",VERTEX,{"disambiguationData":[OD(1.0)],"derivedFrom":[subQ1,subQ0]})])]});}
            var Q11;
            {var subQ0=sQuery(id+"F0.wireOp",EDGE,"E20");var subQ1=sQuery(id+"F0.wireOp",EDGE,"E9");Q11=makeQuery(id+"F1.opExtrude","SWEPT_EDGE",EDGE,{"disambiguationData":[OSD([subQ1,subQ0]),TDD([makeQuery(id+"F0.imprint","INTERSECT",VERTEX,{"disambiguationData":[OD(0.0)],"derivedFrom":[subQ1,subQ0]})])]});}
            fillet(context, id + "F3", {"entities" : qUnion([Q0, Q1, Q2, Q3, Q4, Q5, Q6, Q7, Q8, Q9, Q10, Q11]), "radius" : 2 * mm, "tangentPropagation" : true, "allowEdgeOverflow" : false});
        }
        {
            var Q0;
            Q0=makeQuery(id+"F1.opExtrude","CAP_EDGE",EDGE,{"disambiguationData":[OSD([sQuery(id+"F0.wireOp",EDGE,"E18")])],"isStart":true});
            var Q1;
            {var subQ0=sQuery(id+"F0.wireOp",EDGE,"E9");var subQ1=makeQuery(id+"F0.imprint","INTERSECT",VERTEX,{"derivedFrom":[sQuery(id+"F0.wireOp",EDGE,"E6"),subQ0]});Q1=makeQuery(id+"F1.opExtrude","CAP_EDGE",EDGE,{"disambiguationData":[OSD([subQ0]),TDD([makeQuery(id+"F0.imprint","IMPRINT",EDGE,{"disambiguationData":[TD([[subQ1,1.0]])],"derivedFrom":subQ0}),makeQuery(id+"F0.imprint","IMPRINT",EDGE,{"disambiguationData":[TD([[subQ1,-1.0]])],"derivedFrom":subQ0})])],"isStart":true});}
            var Q2;
            Q2=makeQuery(id+"F1.opExtrude","CAP_EDGE",EDGE,{"disambiguationData":[OSD([sQuery(id+"F0.wireOp",EDGE,"ybPrvi5P-VunJ-4jWC-Pnkx-XrBZV12RTwSU")])],"isStart":true});
            var Q3;
            Q3=makeQuery(id+"F1.opExtrude","CAP_EDGE",EDGE,{"disambiguationData":[OSD([sQuery(id+"F0.wireOp",EDGE,"Z31AIPb3-Qnal-9L9K-KWPF-0pA5MV0Y2tzz")])],"isStart":true});
            var Q4;
            Q4=makeQuery(id+"F1.opExtrude","CAP_EDGE",EDGE,{"disambiguationData":[OSD([sQuery(id+"F0.wireOp",EDGE,"PnXZhhwe-JsCa-7CxD-iQOa-k5J0qBTIRsT0")])],"isStart":true});
            var Q5;
            Q5=makeQuery(id+"F1.opExtrude","CAP_EDGE",EDGE,{"disambiguationData":[OSD([sQuery(id+"F0.wireOp",EDGE,"NqLbyCLt-QwBI-9MIB-e1Nx-km0DvbRRgn6a")])],"isStart":true});
            var Q6;
            Q6=makeQuery(id+"F1.opExtrude","CAP_EDGE",EDGE,{"disambiguationData":[OSD([sQuery(id+"F0.wireOp",EDGE,"FrVRpejz-aWTZ-dKt5-0AgZ-ki6dz13qyr7O")])],"isStart":true});
            var Q7;
            Q7=makeQuery(id+"F1.opExtrude","CAP_EDGE",EDGE,{"disambiguationData":[OSD([sQuery(id+"F0.wireOp",EDGE,"33CorVpG-yTT2-nvUV-cjIG-PMlhWEX7tbI9")])],"isStart":true});
            fillet(context, id + "F4", {"entities" : qUnion([Q0, Q1, Q2, Q3, Q4, Q5, Q6, Q7]), "radius" : 2 * mm, "tangentPropagation" : true, "allowEdgeOverflow" : false});
        }
        {
            var Q0;
            Q0=makeQuery(id+"F1.opExtrude","CAP_EDGE",EDGE,{"disambiguationData":[OSD([sQuery(id+"F0.wireOp",EDGE,"E27.2")])],"isStart":true});
            var Q1;
            Q1=makeQuery(id+"F1.opExtrude","CAP_EDGE",EDGE,{"disambiguationData":[OSD([sQuery(id+"F0.wireOp",EDGE,"E27.3")])],"isStart":true});
            var Q2;
            Q2=makeQuery(id+"F1.opExtrude","CAP_EDGE",EDGE,{"disambiguationData":[OSD([sQuery(id+"F0.wireOp",EDGE,"E26.5")])],"isStart":true});
            var Q3;
            Q3=makeQuery(id+"F1.opExtrude","CAP_EDGE",EDGE,{"disambiguationData":[OSD([sQuery(id+"F0.wireOp",EDGE,"E25.1")])],"isStart":true});
            var Q4;
            Q4=makeQuery(id+"F1.opExtrude","CAP_EDGE",EDGE,{"disambiguationData":[OSD([sQuery(id+"F0.wireOp",EDGE,"E24.0")])],"isStart":true});
            var Q5;
            Q5=makeQuery(id+"F1.opExtrude","CAP_EDGE",EDGE,{"disambiguationData":[OSD([sQuery(id+"F0.wireOp",EDGE,"E23.1")])],"isStart":true});
            var Q6;
            Q6=makeQuery(id+"F1.opExtrude","CAP_EDGE",EDGE,{"disambiguationData":[OSD([sQuery(id+"F0.wireOp",EDGE,"E23.1")])],"isStart":false});
            var Q7;
            Q7=makeQuery(id+"F1.opExtrude","CAP_EDGE",EDGE,{"disambiguationData":[OSD([sQuery(id+"F0.wireOp",EDGE,"E24.1")])],"isStart":false});
            var Q8;
            Q8=makeQuery(id+"F1.opExtrude","CAP_EDGE",EDGE,{"disambiguationData":[OSD([sQuery(id+"F0.wireOp",EDGE,"E22.4")])],"isStart":true});
            var Q9;
            Q9=makeQuery(id+"F1.opExtrude","CAP_EDGE",EDGE,{"disambiguationData":[OSD([sQuery(id+"F0.wireOp",EDGE,"E22.4")])],"isStart":false});
            var Q10;
            Q10=makeQuery(id+"F1.opExtrude","CAP_EDGE",EDGE,{"disambiguationData":[OSD([sQuery(id+"F0.wireOp",EDGE,"E26.5")])],"isStart":false});
            var Q11;
            Q11=makeQuery(id+"F1.opExtrude","CAP_EDGE",EDGE,{"disambiguationData":[OSD([sQuery(id+"F0.wireOp",EDGE,"E27.4")])],"isStart":false});
            var Q12;
            Q12=makeQuery(id+"F1.opExtrude","CAP_EDGE",EDGE,{"disambiguationData":[OSD([sQuery(id+"F0.wireOp",EDGE,"E25.0")])],"isStart":false});
            var Q13;
            Q13=makeQuery(id+"F1.opExtrude","CAP_EDGE",EDGE,{"disambiguationData":[OSD([sQuery(id+"F0.wireOp",EDGE,"E24.0")])],"isStart":false});
            var Q14;
            Q14=makeQuery(id+"F1.opExtrude","CAP_EDGE",EDGE,{"disambiguationData":[OSD([sQuery(id+"F0.wireOp",EDGE,"E24.5")])],"isStart":false});
            var Q15;
            Q15=makeQuery(id+"F1.opExtrude","CAP_EDGE",EDGE,{"disambiguationData":[OSD([sQuery(id+"F0.wireOp",EDGE,"E24.2")])],"isStart":false});
            var Q16;
            Q16=makeQuery(id+"F1.opExtrude","CAP_EDGE",EDGE,{"disambiguationData":[OSD([sQuery(id+"F0.wireOp",EDGE,"E24.3")])],"isStart":false});
            var Q17;
            Q17=makeQuery(id+"F1.opExtrude","CAP_EDGE",EDGE,{"disambiguationData":[OSD([sQuery(id+"F0.wireOp",EDGE,"E24.4")])],"isStart":false});
            var Q18;
            Q18=makeQuery(id+"F1.opExtrude","CAP_EDGE",EDGE,{"disambiguationData":[OSD([sQuery(id+"F0.wireOp",EDGE,"E23.2")])],"isStart":false});
            var Q19;
            Q19=makeQuery(id+"F1.opExtrude","CAP_EDGE",EDGE,{"disambiguationData":[OSD([sQuery(id+"F0.wireOp",EDGE,"E23.2")])],"isStart":true});
            var Q20;
            Q20=makeQuery(id+"F1.opExtrude","CAP_EDGE",EDGE,{"disambiguationData":[OSD([sQuery(id+"F0.wireOp",EDGE,"E23.3")])],"isStart":true});
            var Q21;
            Q21=makeQuery(id+"F1.opExtrude","CAP_EDGE",EDGE,{"disambiguationData":[OSD([sQuery(id+"F0.wireOp",EDGE,"E23.3")])],"isStart":false});
            var Q22;
            Q22=makeQuery(id+"F1.opExtrude","CAP_EDGE",EDGE,{"disambiguationData":[OSD([sQuery(id+"F0.wireOp",EDGE,"E23.5")])],"isStart":false});
            var Q23;
            Q23=makeQuery(id+"F1.opExtrude","CAP_EDGE",EDGE,{"disambiguationData":[OSD([sQuery(id+"F0.wireOp",EDGE,"E23.4")])],"isStart":false});
            var Q24;
            Q24=makeQuery(id+"F1.opExtrude","CAP_EDGE",EDGE,{"disambiguationData":[OSD([sQuery(id+"F0.wireOp",EDGE,"E23.0")])],"isStart":false});
            var Q25;
            Q25=makeQuery(id+"F1.opExtrude","CAP_EDGE",EDGE,{"disambiguationData":[OSD([sQuery(id+"F0.wireOp",EDGE,"E22.3")])],"isStart":true});
            var Q26;
            Q26=makeQuery(id+"F1.opExtrude","CAP_EDGE",EDGE,{"disambiguationData":[OSD([sQuery(id+"F0.wireOp",EDGE,"E22.2")])],"isStart":true});
            var Q27;
            Q27=makeQuery(id+"F1.opExtrude","CAP_EDGE",EDGE,{"disambiguationData":[OSD([sQuery(id+"F0.wireOp",EDGE,"E22.1")])],"isStart":false});
            var Q28;
            Q28=makeQuery(id+"F1.opExtrude","CAP_EDGE",EDGE,{"disambiguationData":[OSD([sQuery(id+"F0.wireOp",EDGE,"E22.0")])],"isStart":false});
            var Q29;
            Q29=makeQuery(id+"F1.opExtrude","CAP_EDGE",EDGE,{"disambiguationData":[OSD([sQuery(id+"F0.wireOp",EDGE,"E22.5")])],"isStart":false});
            var Q30;
            Q30=makeQuery(id+"F1.opExtrude","CAP_EDGE",EDGE,{"disambiguationData":[OSD([sQuery(id+"F0.wireOp",EDGE,"E22.3")])],"isStart":false});
            var Q31;
            Q31=makeQuery(id+"F1.opExtrude","CAP_EDGE",EDGE,{"disambiguationData":[OSD([sQuery(id+"F0.wireOp",EDGE,"E27.4")])],"isStart":true});
            var Q32;
            Q32=makeQuery(id+"F1.opExtrude","CAP_EDGE",EDGE,{"disambiguationData":[OSD([sQuery(id+"F0.wireOp",EDGE,"E27.5")])],"isStart":true});
            var Q33;
            Q33=makeQuery(id+"F1.opExtrude","CAP_EDGE",EDGE,{"disambiguationData":[OSD([sQuery(id+"F0.wireOp",EDGE,"E27.3")])],"isStart":false});
            var Q34;
            Q34=makeQuery(id+"F1.opExtrude","CAP_EDGE",EDGE,{"disambiguationData":[OSD([sQuery(id+"F0.wireOp",EDGE,"E27.2")])],"isStart":false});
            var Q35;
            Q35=makeQuery(id+"F1.opExtrude","CAP_EDGE",EDGE,{"disambiguationData":[OSD([sQuery(id+"F0.wireOp",EDGE,"E27.1")])],"isStart":false});
            var Q36;
            Q36=makeQuery(id+"F1.opExtrude","CAP_EDGE",EDGE,{"disambiguationData":[OSD([sQuery(id+"F0.wireOp",EDGE,"E27.0")])],"isStart":false});
            var Q37;
            Q37=makeQuery(id+"F1.opExtrude","CAP_EDGE",EDGE,{"disambiguationData":[OSD([sQuery(id+"F0.wireOp",EDGE,"E27.5")])],"isStart":false});
            var Q38;
            Q38=makeQuery(id+"F1.opExtrude","CAP_EDGE",EDGE,{"disambiguationData":[OSD([sQuery(id+"F0.wireOp",EDGE,"E26.0")])],"isStart":false});
            var Q39;
            Q39=makeQuery(id+"F1.opExtrude","CAP_EDGE",EDGE,{"disambiguationData":[OSD([sQuery(id+"F0.wireOp",EDGE,"E26.2")])],"isStart":false});
            var Q40;
            Q40=makeQuery(id+"F1.opExtrude","CAP_EDGE",EDGE,{"disambiguationData":[OSD([sQuery(id+"F0.wireOp",EDGE,"E26.1")])],"isStart":false});
            var Q41;
            Q41=makeQuery(id+"F1.opExtrude","CAP_EDGE",EDGE,{"disambiguationData":[OSD([sQuery(id+"F0.wireOp",EDGE,"E26.4")])],"isStart":false});
            var Q42;
            Q42=makeQuery(id+"F1.opExtrude","CAP_EDGE",EDGE,{"disambiguationData":[OSD([sQuery(id+"F0.wireOp",EDGE,"E26.3")])],"isStart":false});
            var Q43;
            Q43=makeQuery(id+"F1.opExtrude","CAP_EDGE",EDGE,{"disambiguationData":[OSD([sQuery(id+"F0.wireOp",EDGE,"E25.4")])],"isStart":false});
            var Q44;
            Q44=makeQuery(id+"F1.opExtrude","CAP_EDGE",EDGE,{"disambiguationData":[OSD([sQuery(id+"F0.wireOp",EDGE,"E25.5")])],"isStart":false});
            var Q45;
            Q45=makeQuery(id+"F1.opExtrude","CAP_EDGE",EDGE,{"disambiguationData":[OSD([sQuery(id+"F0.wireOp",EDGE,"E25.3")])],"isStart":false});
            var Q46;
            Q46=makeQuery(id+"F1.opExtrude","CAP_EDGE",EDGE,{"disambiguationData":[OSD([sQuery(id+"F0.wireOp",EDGE,"E25.2")])],"isStart":false});
            var Q47;
            Q47=makeQuery(id+"F1.opExtrude","CAP_EDGE",EDGE,{"disambiguationData":[OSD([sQuery(id+"F0.wireOp",EDGE,"E26.1")])],"isStart":true});
            var Q48;
            Q48=makeQuery(id+"F1.opExtrude","CAP_EDGE",EDGE,{"disambiguationData":[OSD([sQuery(id+"F0.wireOp",EDGE,"E26.0")])],"isStart":true});
            var Q49;
            Q49=makeQuery(id+"F1.opExtrude","CAP_EDGE",EDGE,{"disambiguationData":[OSD([sQuery(id+"F0.wireOp",EDGE,"E26.2")])],"isStart":true});
            var Q50;
            Q50=makeQuery(id+"F1.opExtrude","CAP_EDGE",EDGE,{"disambiguationData":[OSD([sQuery(id+"F0.wireOp",EDGE,"E26.4")])],"isStart":true});
            var Q51;
            Q51=makeQuery(id+"F1.opExtrude","CAP_EDGE",EDGE,{"disambiguationData":[OSD([sQuery(id+"F0.wireOp",EDGE,"E26.3")])],"isStart":true});
            var Q52;
            Q52=makeQuery(id+"F1.opExtrude","CAP_EDGE",EDGE,{"disambiguationData":[OSD([sQuery(id+"F0.wireOp",EDGE,"E27.1")])],"isStart":true});
            var Q53;
            Q53=makeQuery(id+"F1.opExtrude","CAP_EDGE",EDGE,{"disambiguationData":[OSD([sQuery(id+"F0.wireOp",EDGE,"E27.0")])],"isStart":true});
            var Q54;
            Q54=makeQuery(id+"F1.opExtrude","CAP_EDGE",EDGE,{"disambiguationData":[OSD([sQuery(id+"F0.wireOp",EDGE,"E25.1")])],"isStart":false});
            var Q55;
            Q55=makeQuery(id+"F1.opExtrude","CAP_EDGE",EDGE,{"disambiguationData":[OSD([sQuery(id+"F0.wireOp",EDGE,"E23.5")])],"isStart":true});
            var Q56;
            Q56=makeQuery(id+"F1.opExtrude","CAP_EDGE",EDGE,{"disambiguationData":[OSD([sQuery(id+"F0.wireOp",EDGE,"E23.0")])],"isStart":true});
            var Q57;
            Q57=makeQuery(id+"F1.opExtrude","CAP_EDGE",EDGE,{"disambiguationData":[OSD([sQuery(id+"F0.wireOp",EDGE,"E23.4")])],"isStart":true});
            var Q58;
            Q58=makeQuery(id+"F1.opExtrude","CAP_EDGE",EDGE,{"disambiguationData":[OSD([sQuery(id+"F0.wireOp",EDGE,"E24.2")])],"isStart":true});
            var Q59;
            Q59=makeQuery(id+"F1.opExtrude","CAP_EDGE",EDGE,{"disambiguationData":[OSD([sQuery(id+"F0.wireOp",EDGE,"E24.1")])],"isStart":true});
            var Q60;
            Q60=makeQuery(id+"F1.opExtrude","CAP_EDGE",EDGE,{"disambiguationData":[OSD([sQuery(id+"F0.wireOp",EDGE,"E24.3")])],"isStart":true});
            var Q61;
            Q61=makeQuery(id+"F1.opExtrude","CAP_EDGE",EDGE,{"disambiguationData":[OSD([sQuery(id+"F0.wireOp",EDGE,"E24.4")])],"isStart":true});
            var Q62;
            Q62=makeQuery(id+"F1.opExtrude","CAP_EDGE",EDGE,{"disambiguationData":[OSD([sQuery(id+"F0.wireOp",EDGE,"E24.5")])],"isStart":true});
            var Q63;
            Q63=makeQuery(id+"F1.opExtrude","CAP_EDGE",EDGE,{"disambiguationData":[OSD([sQuery(id+"F0.wireOp",EDGE,"E25.0")])],"isStart":true});
            var Q64;
            Q64=makeQuery(id+"F1.opExtrude","CAP_EDGE",EDGE,{"disambiguationData":[OSD([sQuery(id+"F0.wireOp",EDGE,"E25.5")])],"isStart":true});
            var Q65;
            Q65=makeQuery(id+"F1.opExtrude","CAP_EDGE",EDGE,{"disambiguationData":[OSD([sQuery(id+"F0.wireOp",EDGE,"E25.4")])],"isStart":true});
            var Q66;
            Q66=makeQuery(id+"F1.opExtrude","CAP_EDGE",EDGE,{"disambiguationData":[OSD([sQuery(id+"F0.wireOp",EDGE,"E25.3")])],"isStart":true});
            var Q67;
            Q67=makeQuery(id+"F1.opExtrude","CAP_EDGE",EDGE,{"disambiguationData":[OSD([sQuery(id+"F0.wireOp",EDGE,"E25.2")])],"isStart":true});
            var Q68;
            Q68=makeQuery(id+"F1.opExtrude","CAP_EDGE",EDGE,{"disambiguationData":[OSD([sQuery(id+"F0.wireOp",EDGE,"E22.0")])],"isStart":true});
            var Q69;
            Q69=makeQuery(id+"F1.opExtrude","CAP_EDGE",EDGE,{"disambiguationData":[OSD([sQuery(id+"F0.wireOp",EDGE,"E22.5")])],"isStart":true});
            var Q70;
            Q70=makeQuery(id+"F1.opExtrude","CAP_EDGE",EDGE,{"disambiguationData":[OSD([sQuery(id+"F0.wireOp",EDGE,"E22.2")])],"isStart":false});
            var Q71;
            Q71=makeQuery(id+"F1.opExtrude","CAP_EDGE",EDGE,{"disambiguationData":[OSD([sQuery(id+"F0.wireOp",EDGE,"E22.1")])],"isStart":true});
            fillet(context, id + "F5", {"entities" : qUnion([Q0, Q1, Q2, Q3, Q4, Q5, Q6, Q7, Q8, Q9, Q10, Q11, Q12, Q13, Q14, Q15, Q16, Q17, Q18, Q19, Q20, Q21, Q22, Q23, Q24, Q25, Q26, Q27, Q28, Q29, Q30, Q31, Q32, Q33, Q34, Q35, Q36, Q37, Q38, Q39, Q40, Q41, Q42, Q43, Q44, Q45, Q46, Q47, Q48, Q49, Q50, Q51, Q52, Q53, Q54, Q55, Q56, Q57, Q58, Q59, Q60, Q61, Q62, Q63, Q64, Q65, Q66, Q67, Q68, Q69, Q70, Q71]), "radius" : 0.5 * mm, "tangentPropagation" : true, "allowEdgeOverflow" : false});
        }
        {
            var Q0;
            Q0=makeQuery(id+"F1.opExtrude","CAP_EDGE",EDGE,{"disambiguationData":[OSD([sQuery(id+"F0.wireOp",EDGE,"E0")])],"isStart":false});
            var Q1;
            Q1=makeQuery(id+"F1.opExtrude","CAP_EDGE",EDGE,{"disambiguationData":[OSD([sQuery(id+"F0.wireOp",EDGE,"E0")])],"isStart":true});
            fillet(context, id + "F6", {"entities" : qUnion([Q0, Q1]), "radius" : 0.5 * mm, "tangentPropagation" : true, "allowEdgeOverflow" : false});
        }
    });
